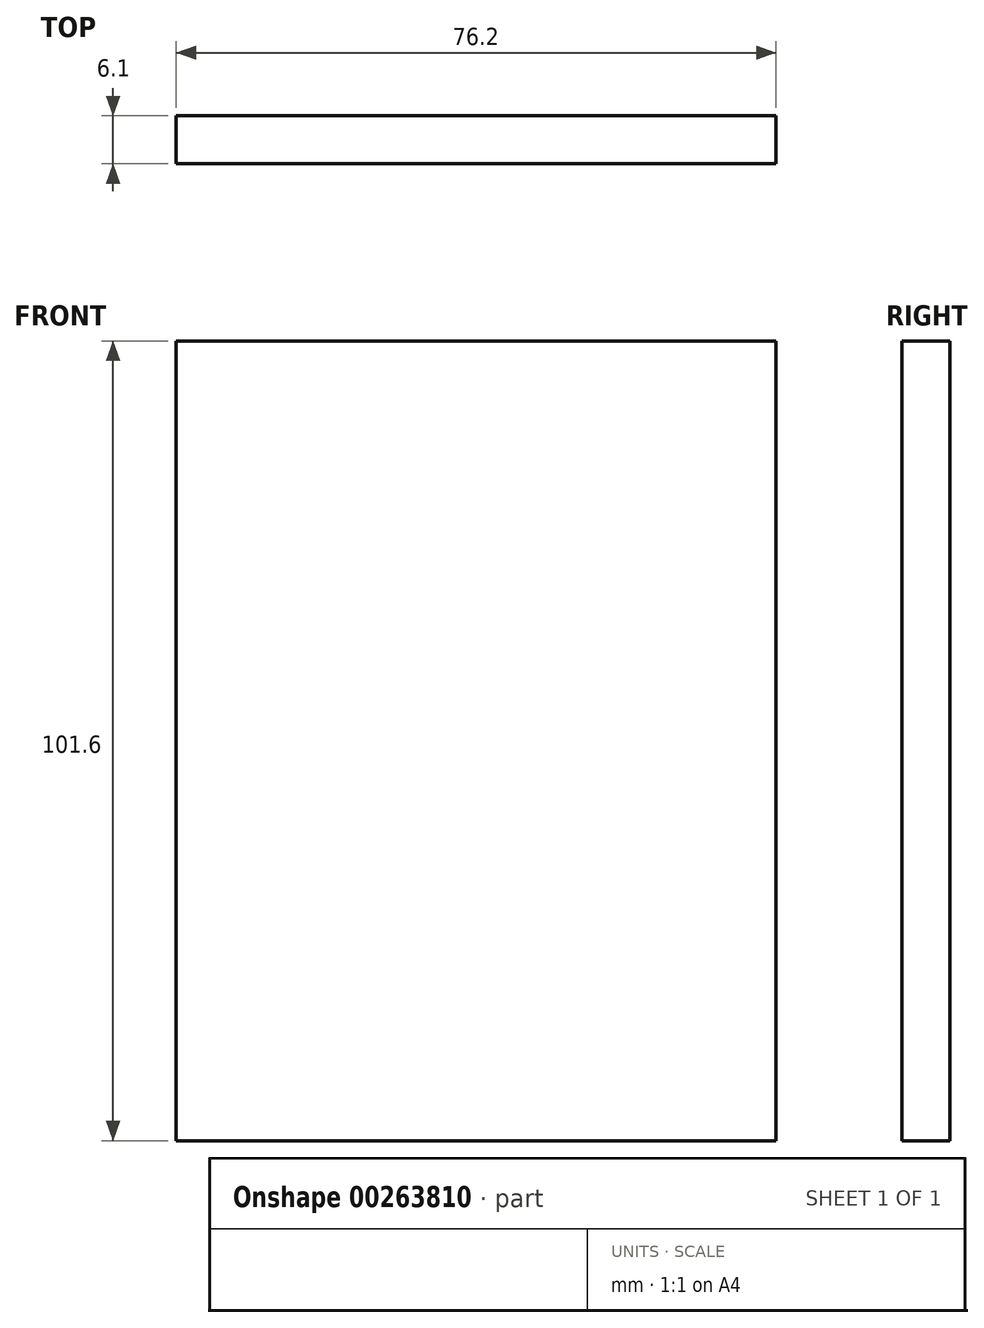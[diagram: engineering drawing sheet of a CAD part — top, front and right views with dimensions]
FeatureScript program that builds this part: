
annotation { "Feature Type Name" : "Feature", "Feature Type Description" : "" }
export const myFeature = defineFeature(function(context is Context, id is Id, definition is map)
    precondition{}
    {
        {
            var Q0;
            Q0=qCreatedBy(makeId("Front.planeOp"),FACE);
            var sketch = newSketch(context, id + "F0", { "sketchPlane" : qUnion([Q0])});
            skLineSegment(sketch, "E0.bottom", {"start": v(38.1, 50.8) * mm, "end": v(-38.1, 50.8) * mm});
            skLineSegment(sketch, "E0.top", {"start": v(38.1, -50.8) * mm, "end": v(-38.1, -50.8) * mm});
            skLineSegment(sketch, "E0.left", {"start": v(38.1, 50.8) * mm, "end": v(38.1, -50.8) * mm});
            skLineSegment(sketch, "E0.right", {"start": v(-38.1, 50.8) * mm, "end": v(-38.1, -50.8) * mm});
            skPoint(sketch, "E0.middle", {"position": v(0, 0) * mm});
            skSolve(sketch);
        }
        {
            var Q0;
            Q0 = qSketchRegion(id + "F0", true);
            extrude(context, id + "F1", {"entities" : qUnion([Q0]), "depth" : 6.1 * mm});
        }
    });
